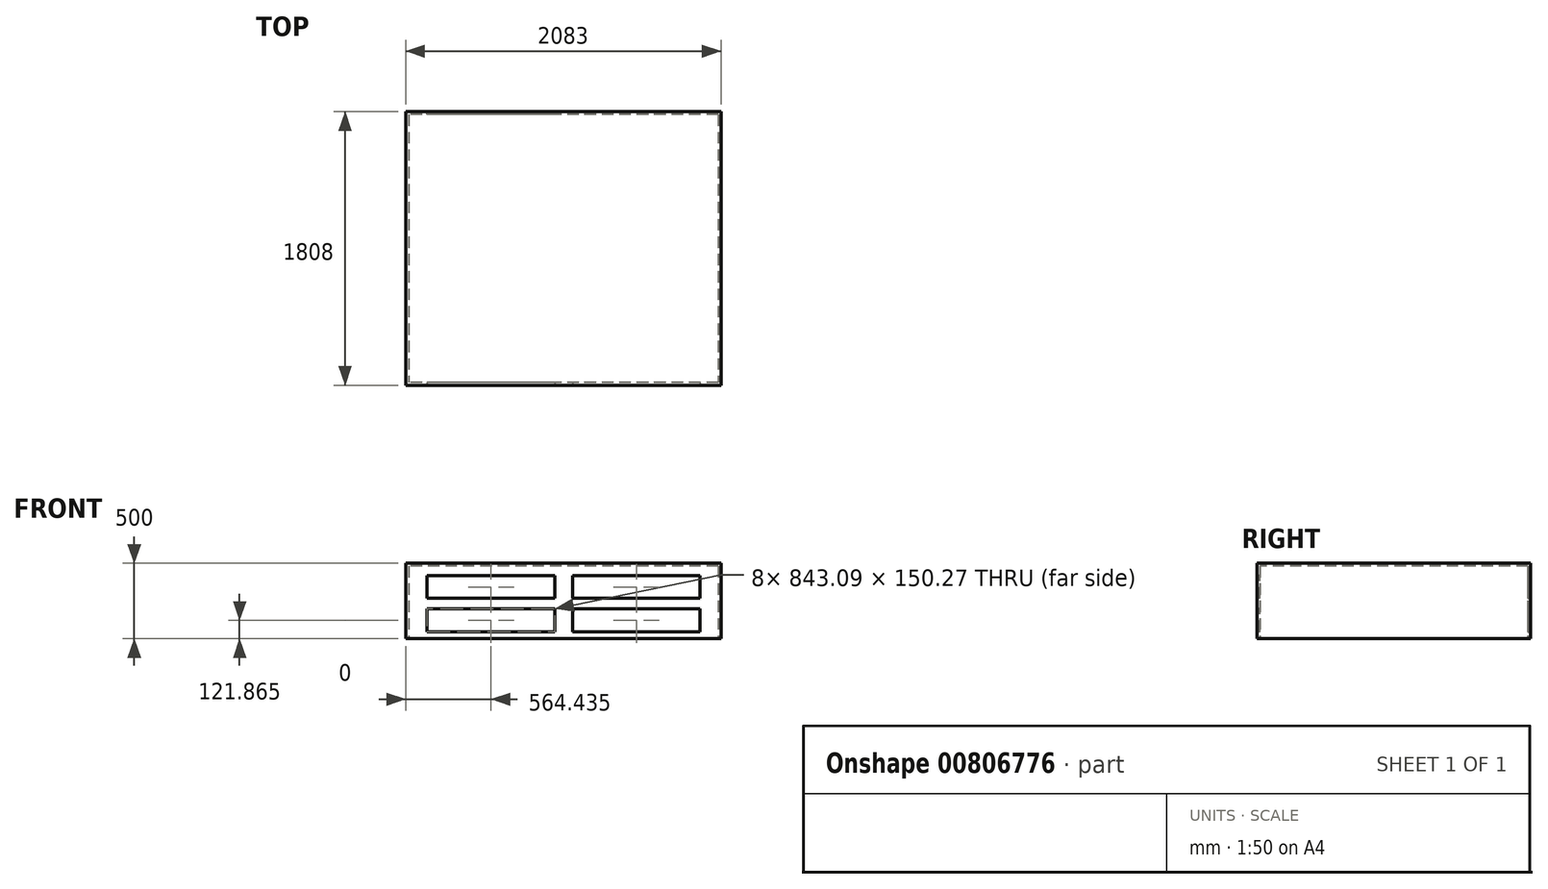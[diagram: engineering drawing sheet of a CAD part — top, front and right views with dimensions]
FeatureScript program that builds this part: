
annotation { "Feature Type Name" : "Feature", "Feature Type Description" : "" }
export const myFeature = defineFeature(function(context is Context, id is Id, definition is map)
    precondition{}
    {
        {
            var Q0;
            Q0=qCreatedBy(makeId("Top.planeOp"),FACE);
            var sketch = newSketch(context, id + "F0", { "sketchPlane" : qUnion([Q0])});
            skLineSegment(sketch, "E0.bottom", {"start": v(1041.5, 904) * mm, "end": v(-1041.5, 904) * mm});
            skLineSegment(sketch, "E0.top", {"start": v(1041.5, -904) * mm, "end": v(-1041.5, -904) * mm});
            skLineSegment(sketch, "E0.left", {"start": v(1041.5, 904) * mm, "end": v(1041.5, -904) * mm});
            skLineSegment(sketch, "E0.right", {"start": v(-1041.5, 904) * mm, "end": v(-1041.5, -904) * mm});
            skPoint(sketch, "E0.middle", {"position": v(0, 0) * mm});
            skSolve(sketch);
        }
        {
            var Q0;
            Q0=makeQuery(id+"F0.imprint","IMPRINT",FACE,{"disambiguationData":[TD([[makeQuery(id+"F0.imprint","IMPRINT",EDGE,{"derivedFrom":sQuery(id+"F0.wireOp",EDGE,"E0.bottom")}),1.0]])]});
            extrude(context, id + "F1", {"entities" : qUnion([Q0]), "depth" : 500 * mm, "offsetDistance" : 25 * mm});
        }
        {
            var Q0;
            Q0=makeQuery(id+"F1.opExtrude","CAP_FACE",FACE,{"disambiguationData":[OSD([sQuery(id+"F0.wireOp",EDGE,"E0.bottom"),sQuery(id+"F0.wireOp",EDGE,"E0.top"),sQuery(id+"F0.wireOp",EDGE,"E0.left"),sQuery(id+"F0.wireOp",EDGE,"E0.right")])],"isStart":true});
            shell(context, id + "F2", {"entities" : qUnion([Q0]), "thickness" : 19 * mm});
        }
        {
            var Q0;
            Q0=makeQuery(id+"F1.opExtrude","SWEPT_FACE",FACE,{"disambiguationData":[OSD([sQuery(id+"F0.wireOp",EDGE,"E0.top")])]});
            var sketch = newSketch(context, id + "F3", { "sketchPlane" : qUnion([Q0])});
            skLineSegment(sketch, "E1.bottom", {"start": v(-898.6, 417) * mm, "end": v(-55.52, 417) * mm});
            skLineSegment(sketch, "E1.top", {"start": v(-898.6, 266.73) * mm, "end": v(-55.52, 266.73) * mm});
            skLineSegment(sketch, "E1.left", {"start": v(-898.6, 417) * mm, "end": v(-898.6, 266.73) * mm});
            skLineSegment(sketch, "E1.right", {"start": v(-55.52, 417) * mm, "end": v(-55.52, 266.73) * mm});
            skLineSegment(sketch, "E2.0.1.0", {"start": v(-55.52, 197) * mm, "end": v(-55.52, 46.73) * mm});
            skLineSegment(sketch, "E2.0.1.1", {"start": v(-898.6, 197) * mm, "end": v(-55.52, 197) * mm});
            skLineSegment(sketch, "E2.0.1.2", {"start": v(-898.6, 46.73) * mm, "end": v(-55.52, 46.73) * mm});
            skLineSegment(sketch, "E2.0.1.3", {"start": v(-898.6, 197) * mm, "end": v(-898.6, 46.73) * mm});
            skLineSegment(sketch, "E2.1.0.0", {"start": v(904.48, 417) * mm, "end": v(904.48, 266.73) * mm});
            skLineSegment(sketch, "E2.1.0.1", {"start": v(61.4, 417) * mm, "end": v(904.48, 417) * mm});
            skLineSegment(sketch, "E2.1.0.2", {"start": v(61.4, 266.73) * mm, "end": v(904.48, 266.73) * mm});
            skLineSegment(sketch, "E2.1.0.3", {"start": v(61.4, 417) * mm, "end": v(61.4, 266.73) * mm});
            skLineSegment(sketch, "E2.1.1.0", {"start": v(904.48, 197) * mm, "end": v(904.48, 46.73) * mm});
            skLineSegment(sketch, "E2.1.1.1", {"start": v(61.4, 197) * mm, "end": v(904.48, 197) * mm});
            skLineSegment(sketch, "E2.1.1.2", {"start": v(61.4, 46.73) * mm, "end": v(904.48, 46.73) * mm});
            skLineSegment(sketch, "E2.1.1.3", {"start": v(61.4, 197) * mm, "end": v(61.4, 46.73) * mm});
            skLineSegment(sketch, "E2.direction1", {"start": v(-55.52, 266.73) * mm, "end": v(904.48, 266.73) * mm, "construction": true});
            skLineSegment(sketch, "E2.direction2", {"start": v(-55.52, 266.73) * mm, "end": v(-55.52, 46.73) * mm, "construction": true});
            skSolve(sketch);
        }
        {
            var Q0;
            Q0=makeQuery(id+"F3.imprint","IMPRINT",FACE,{"disambiguationData":[TD([[makeQuery(id+"F3.imprint","IMPRINT",EDGE,{"derivedFrom":sQuery(id+"F3.wireOp",EDGE,"E1.bottom")}),-1.0]])]});
            var Q1;
            Q1=makeQuery(id+"F3.imprint","IMPRINT",FACE,{"disambiguationData":[TD([[makeQuery(id+"F3.imprint","IMPRINT",EDGE,{"derivedFrom":sQuery(id+"F3.wireOp",EDGE,"E2.1.0.0")}),-1.0]])]});
            var Q2;
            Q2=makeQuery(id+"F3.imprint","IMPRINT",FACE,{"disambiguationData":[TD([[makeQuery(id+"F3.imprint","IMPRINT",EDGE,{"derivedFrom":sQuery(id+"F3.wireOp",EDGE,"E2.0.1.0")}),-1.0]])]});
            var Q3;
            Q3=makeQuery(id+"F3.imprint","IMPRINT",FACE,{"disambiguationData":[TD([[makeQuery(id+"F3.imprint","IMPRINT",EDGE,{"derivedFrom":sQuery(id+"F3.wireOp",EDGE,"E2.1.1.0")}),-1.0]])]});
            extrude(context, id + "F4", {"entities" : qUnion([Q0, Q1, Q2, Q3]), "operationType" : NewBodyOperationType.REMOVE, "endBound" : BoundingType.UP_TO_NEXT, "oppositeDirection" : true, "depth" : 25 * mm, "offsetDistance" : 25 * mm});
        }
        {
            var Q0;
            Q0=makeQuery(id+"F1.opExtrude","SWEPT_FACE",FACE,{"disambiguationData":[OSD([sQuery(id+"F0.wireOp",EDGE,"E0.bottom")])]});
            var sketch = newSketch(context, id + "F5", { "sketchPlane" : qUnion([Q0])});
            skPoint(sketch, "E3.0", {"position": v(-904.48, 417) * mm});
            skPoint(sketch, "E4.0", {"position": v(-61.4, 266.73) * mm});
            skPoint(sketch, "E5.0", {"position": v(-904.48, 197) * mm});
            skPoint(sketch, "E6.0", {"position": v(-61.4, 46.73) * mm});
            skPoint(sketch, "E7.0", {"position": v(55.52, 197) * mm});
            skPoint(sketch, "E8.0", {"position": v(898.6, 46.73) * mm});
            skPoint(sketch, "E9.0", {"position": v(898.6, 266.73) * mm});
            skPoint(sketch, "E10.0", {"position": v(55.52, 417) * mm});
            skLineSegment(sketch, "E11.bottom", {"start": v(-904.48, 417) * mm, "end": v(-61.4, 417) * mm});
            skLineSegment(sketch, "E11.top", {"start": v(-904.48, 266.73) * mm, "end": v(-61.4, 266.73) * mm});
            skLineSegment(sketch, "E11.left", {"start": v(-904.48, 417) * mm, "end": v(-904.48, 266.73) * mm});
            skLineSegment(sketch, "E11.right", {"start": v(-61.4, 417) * mm, "end": v(-61.4, 266.73) * mm});
            skLineSegment(sketch, "E12.bottom", {"start": v(55.52, 417) * mm, "end": v(898.6, 417) * mm});
            skLineSegment(sketch, "E12.top", {"start": v(55.52, 266.73) * mm, "end": v(898.6, 266.73) * mm});
            skLineSegment(sketch, "E12.left", {"start": v(55.52, 417) * mm, "end": v(55.52, 266.73) * mm});
            skLineSegment(sketch, "E12.right", {"start": v(898.6, 417) * mm, "end": v(898.6, 266.73) * mm});
            skLineSegment(sketch, "E13.bottom", {"start": v(55.52, 197) * mm, "end": v(898.6, 197) * mm});
            skLineSegment(sketch, "E13.top", {"start": v(55.52, 46.73) * mm, "end": v(898.6, 46.73) * mm});
            skLineSegment(sketch, "E13.left", {"start": v(55.52, 197) * mm, "end": v(55.52, 46.73) * mm});
            skLineSegment(sketch, "E13.right", {"start": v(898.6, 197) * mm, "end": v(898.6, 46.73) * mm});
            skLineSegment(sketch, "E14.bottom", {"start": v(-904.48, 197) * mm, "end": v(-61.4, 197) * mm});
            skLineSegment(sketch, "E14.top", {"start": v(-904.48, 46.73) * mm, "end": v(-61.4, 46.73) * mm});
            skLineSegment(sketch, "E14.left", {"start": v(-904.48, 197) * mm, "end": v(-904.48, 46.73) * mm});
            skLineSegment(sketch, "E14.right", {"start": v(-61.4, 197) * mm, "end": v(-61.4, 46.73) * mm});
            skSolve(sketch);
        }
        {
            var Q0;
            Q0=makeQuery(id+"F5.imprint","IMPRINT",FACE,{"disambiguationData":[TD([[makeQuery(id+"F5.imprint","IMPRINT",EDGE,{"derivedFrom":sQuery(id+"F5.wireOp",EDGE,"E11.bottom")}),-1.0]])]});
            var Q1;
            Q1=makeQuery(id+"F5.imprint","IMPRINT",FACE,{"disambiguationData":[TD([[makeQuery(id+"F5.imprint","IMPRINT",EDGE,{"derivedFrom":sQuery(id+"F5.wireOp",EDGE,"E12.bottom")}),-1.0]])]});
            var Q2;
            Q2=makeQuery(id+"F5.imprint","IMPRINT",FACE,{"disambiguationData":[TD([[makeQuery(id+"F5.imprint","IMPRINT",EDGE,{"derivedFrom":sQuery(id+"F5.wireOp",EDGE,"E14.bottom")}),-1.0]])]});
            var Q3;
            Q3=makeQuery(id+"F5.imprint","IMPRINT",FACE,{"disambiguationData":[TD([[makeQuery(id+"F5.imprint","IMPRINT",EDGE,{"derivedFrom":sQuery(id+"F5.wireOp",EDGE,"E13.bottom")}),-1.0]])]});
            extrude(context, id + "F6", {"entities" : qUnion([Q0, Q1, Q2, Q3]), "operationType" : NewBodyOperationType.REMOVE, "endBound" : BoundingType.UP_TO_NEXT, "oppositeDirection" : true, "depth" : 25 * mm, "offsetDistance" : 25 * mm});
        }
    });
